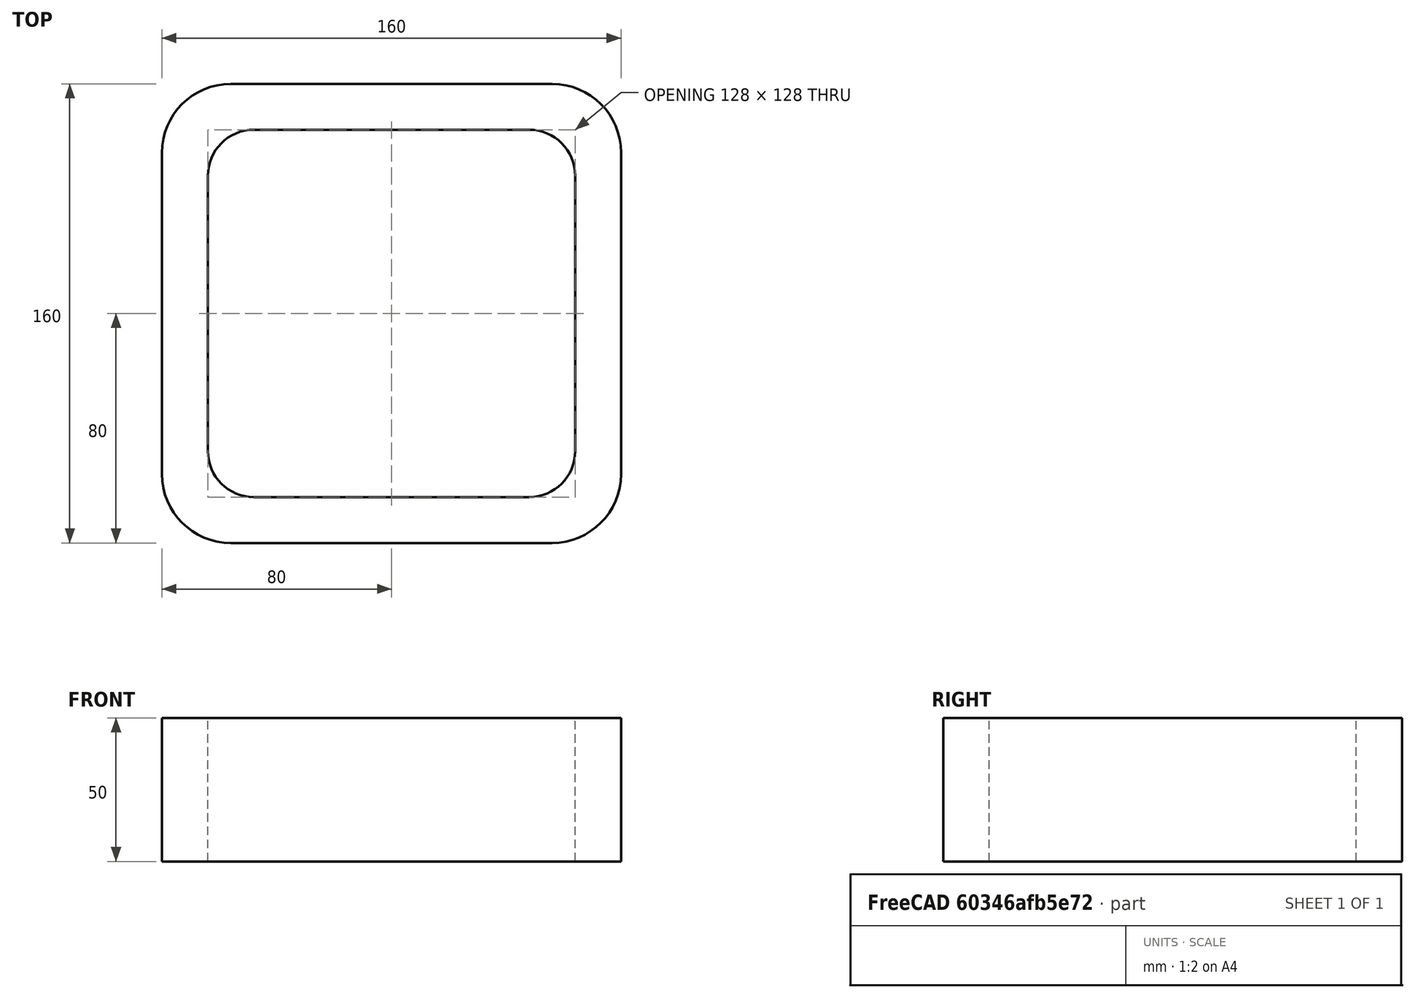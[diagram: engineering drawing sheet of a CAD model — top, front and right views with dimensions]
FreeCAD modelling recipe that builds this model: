
FCSTD DOCUMENT  (FreeCAD 0.15R4671 (Git))
Label: Square hollow section 160x160x16 EN10219 S235JRH
License: All rights reserved
LicenseURL: http://en.wikipedia.org/wiki/All_rights_reserved
objects: Sketcher::SketchObject×1, Part::Extrusion×1
note: 2 computed .brp shape members not serialized (recipe doc carries the construction recipe); baked Part::Feature solids carry a one-line shape summary decoded from their .brp

FEATURE [Sketcher::SketchObject] Sketch
  sketch-geometry (16):
    g0: LineSegment StartX=-48 StartY=64 StartZ=0 EndX=48 EndY=64 EndZ=0
    g1: LineSegment StartX=64 StartY=48 StartZ=0 EndX=64 EndY=-48 EndZ=0
    g2: LineSegment StartX=48 StartY=-64 StartZ=0 EndX=-48 EndY=-64 EndZ=0
    g3: LineSegment StartX=-64 StartY=-48 StartZ=0 EndX=-64 EndY=48 EndZ=0
    g4: LineSegment StartX=-56 StartY=80 StartZ=0 EndX=56 EndY=80 EndZ=0
    g5: LineSegment StartX=80 StartY=56 StartZ=0 EndX=80 EndY=-56 EndZ=0
    g6: LineSegment StartX=56 StartY=-80 StartZ=0 EndX=-56 EndY=-80 EndZ=0
    g7: LineSegment StartX=-80 StartY=-56 StartZ=0 EndX=-80 EndY=56 EndZ=0
    g8: ArcOfCircle CenterX=-48 CenterY=48 CenterZ=0 NormalX=0 NormalY=0 NormalZ=1 Radius=16 StartAngle=1.5708 EndAngle=3.14159
    g9: ArcOfCircle CenterX=48 CenterY=48 CenterZ=0 NormalX=0 NormalY=0 NormalZ=1 Radius=16 StartAngle=0 EndAngle=1.5708
    g10: ArcOfCircle CenterX=48 CenterY=-48 CenterZ=0 NormalX=0 NormalY=0 NormalZ=1 Radius=16 StartAngle=4.71239 EndAngle=6.28319
    g11: ArcOfCircle CenterX=-48 CenterY=-48 CenterZ=0 NormalX=0 NormalY=0 NormalZ=1 Radius=16 StartAngle=3.14159 EndAngle=4.71239
    g12: ArcOfCircle CenterX=56 CenterY=56 CenterZ=0 NormalX=0 NormalY=0 NormalZ=1 Radius=24 StartAngle=0 EndAngle=1.5708
    g13: ArcOfCircle CenterX=56 CenterY=-56 CenterZ=0 NormalX=0 NormalY=0 NormalZ=1 Radius=24 StartAngle=4.71239 EndAngle=6.28319
    g14: ArcOfCircle CenterX=-56 CenterY=-56 CenterZ=0 NormalX=0 NormalY=0 NormalZ=1 Radius=24 StartAngle=3.14159 EndAngle=4.71239
    g15: ArcOfCircle CenterX=-56 CenterY=56 CenterZ=0 NormalX=0 NormalY=0 NormalZ=1 Radius=24 StartAngle=1.5708 EndAngle=3.14159
  constraints (36):
    c: Horizontal(g2)
    c: Vertical(g3)
    c: Horizontal(g6)
    c: Vertical(g7)
    c: Tangent(g3,g8) = 1.5708
    c: Tangent(g0,g8) = 1.5708
    c: Tangent(g0,g9) = 1.5708
    c: Tangent(g1,g9) = 1.5708
    c: Tangent(g1,g10) = 1.5708
    c: Tangent(g2,g10) = 1.5708
    c: Tangent(g2,g11) = 1.5708
    c: Tangent(g3,g11) = 1.5708
    c: Tangent(g4,g12) = 1.5708
    c: Tangent(g5,g12) = 1.5708
    c: Tangent(g5,g13) = 1.5708
    c: Tangent(g6,g13) = 1.5708
    c: Tangent(g6,g14) = 1.5708
    c: Tangent(g7,g14) = 1.5708
    c: Tangent(g7,g15) = 1.5708
    c: Tangent(g4,g15) = 1.5708
    c: Equal(g9,g8)
    c: Equal(g9,g11)
    c: Equal(g9,g10)
    c: Equal(g12,g15)
    c: Equal(g12,g14)
    c: Equal(g12,g13)
    c: Symmetric(g4,g6,g-1)
    c: Symmetric(g7,g5,g-2)
    c: DistanceY(g4,g6) = -160
    c: DistanceX(g7,g5) = 160
    c: Symmetric(g3,g1,g-2)
    c: Symmetric(g0,g2,g-1)
    c: DistanceY(g0,g4) = 16
    c: DistanceX(g5,g1) = -16
    c: Radius(g9) = 16
    c: Radius(g12) = 24
FEATURE [Part::Extrusion] Extrude  label="Square hollow section 160x160x16 EN10219 S235JRH"
  Base = -> Sketch
  Dir = (0,0,50)
  Solid = true
